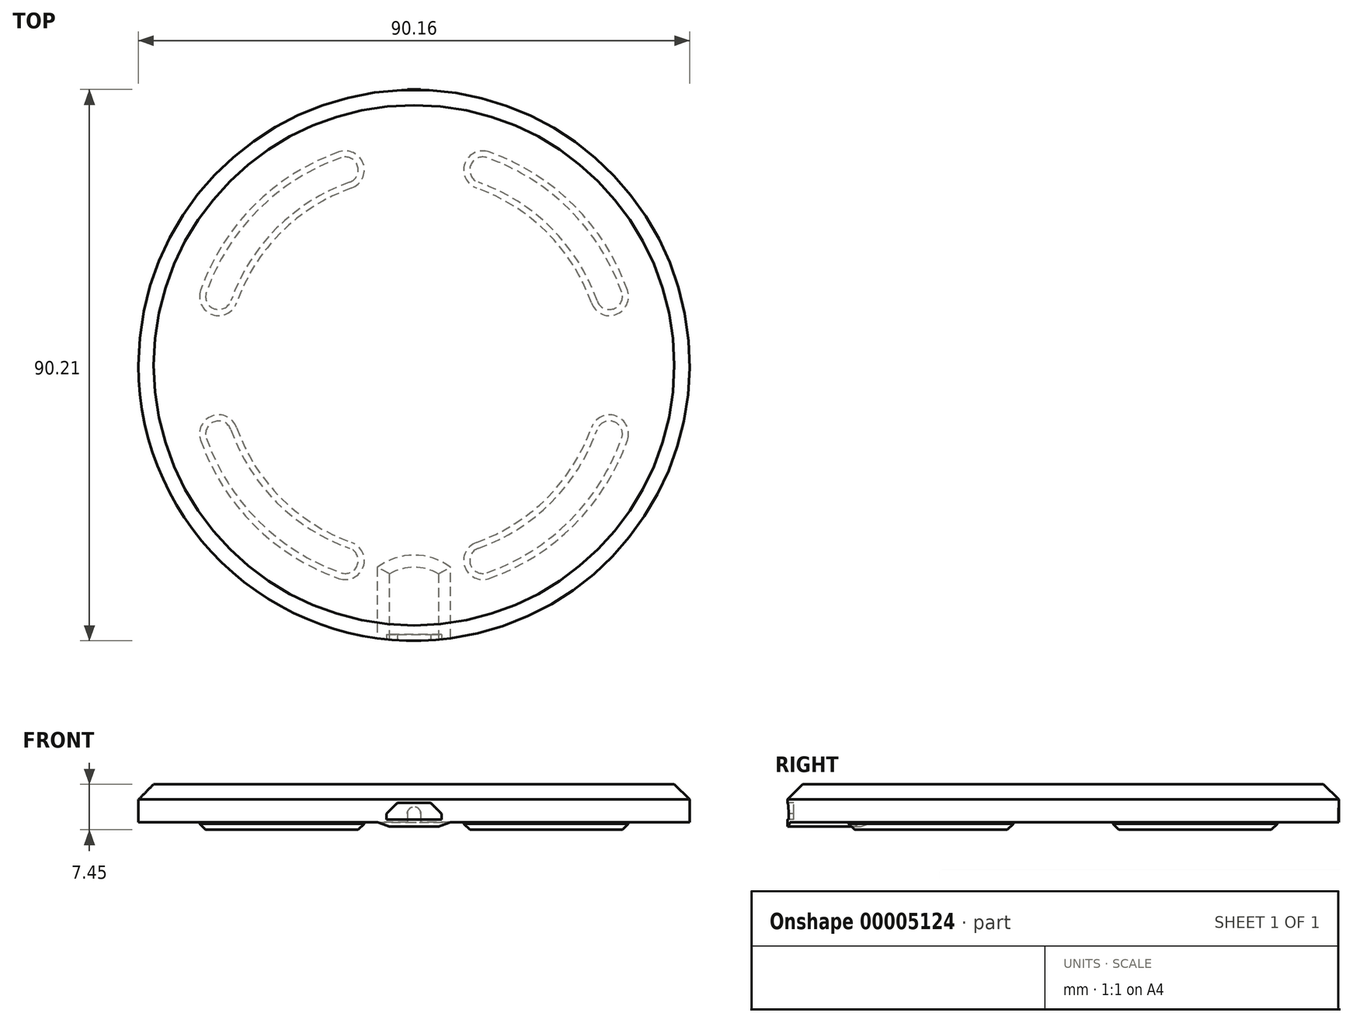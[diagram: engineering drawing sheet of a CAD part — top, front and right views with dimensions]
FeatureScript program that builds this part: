
annotation { "Feature Type Name" : "Feature", "Feature Type Description" : "" }
export const myFeature = defineFeature(function(context is Context, id is Id, definition is map)
    precondition{}
    {
        {
            var Q0;
            Q0=qCreatedBy(makeId("Top.planeOp"),FACE);
            var sketch = newSketch(context, id + "F0", { "sketchPlane" : qUnion([Q0])});
            skCircle(sketch, "E0", {"center": v(0, 0) * mm, "radius": 45.08 * mm});
            skSolve(sketch);
        }
        {
            var Q0;
            Q0 = qSketchRegion(id + "F0", true);
            extrude(context, id + "F1", {"entities" : qUnion([Q0]), "depth" : 6.2 * mm});
        }
        {
            var Q0;
            Q0=makeQuery(id+"F1.opExtrude","CAP_EDGE",EDGE,{"disambiguationData":[OSD([sQuery(id+"F0.wireOp",EDGE,"E0")])],"isStart":false});
            chamfer(context, id + "F2", {"entities" : qUnion([Q0]), "width" : 2.5 * mm, "tangentPropagation" : true});
        }
        {
            var Q0;
            Q0=makeQuery(id+"F1.opExtrude","CAP_FACE",FACE,{"disambiguationData":[OSD([sQuery(id+"F0.wireOp",EDGE,"E0")])],"isStart":true});
            var sketch = newSketch(context, id + "F3", { "sketchPlane" : qUnion([Q0])});
            skCircle(sketch, "E1", {"center": v(0, 0) * mm, "radius": 30.75 * mm});
            skCircle(sketch, "E2", {"center": v(0, 0) * mm, "radius": 37 * mm});
            skLineSegment(sketch, "E3", {"start": v(0, 37) * mm, "end": v(0, 30.75) * mm, "construction": true});
            skPoint(sketch, "E4", {"position": v(0, 30.75) * mm});
            skLineSegment(sketch, "E5", {"start": v(0, 30.75) * mm, "end": v(0, -45.08) * mm, "construction": true});
            skCircle(sketch, "E6", {"center": v(0, 33.88) * mm, "radius": 1 * mm});
            skLineSegment(sketch, "E7", {"start": v(-6, -44.67) * mm, "end": v(-6, -33.08) * mm});
            skLineSegment(sketch, "E8", {"start": v(6, -33.08) * mm, "end": v(6, -44.67) * mm});
            skArc(sketch, "E9", {"start": v(6, -33.08) * mm, "mid": v(0, -31.07) * mm, "end": v(-6, -33.08) * mm});
            skLineSegment(sketch, "E10", {"start": v(-6, -33.08) * mm, "end": v(6, -33.08) * mm, "construction": true});
            skLineSegment(sketch, "E11", {"start": v(0, 0) * mm, "end": v(-37, 0) * mm, "construction": true});
            skLineSegment(sketch, "E12", {"start": v(0, 0) * mm, "end": v(-26.16, 26.16) * mm, "construction": true});
            skLineSegment(sketch, "E13", {"start": v(-35.89, 9.01) * mm, "end": v(-29.82, 7.5) * mm, "construction": true});
            skPoint(sketch, "E14", {"position": v(-32.85, 8.25) * mm});
            skArc(sketch, "E15", {"start": v(-34.9, 12.28) * mm, "mid": v(-33, 8.3) * mm, "end": v(-29, 10.2) * mm});
            skArc(sketch, "E16.0.MirrorCS", {"start": v(-12.28, 34.9) * mm, "mid": v(-8.3, 33) * mm, "end": v(-10.2, 29) * mm});
            skArc(sketch, "E17.1.0", {"start": v(-12.28, -34.9) * mm, "mid": v(-8.3, -33) * mm, "end": v(-10.2, -29) * mm});
            skArc(sketch, "E17.1.1", {"start": v(-34.9, -12.28) * mm, "mid": v(-33, -8.3) * mm, "end": v(-29, -10.2) * mm});
            skArc(sketch, "E17.2.0", {"start": v(34.9, -12.28) * mm, "mid": v(33, -8.3) * mm, "end": v(29, -10.2) * mm});
            skArc(sketch, "E17.2.1", {"start": v(12.28, -34.9) * mm, "mid": v(8.3, -33) * mm, "end": v(10.2, -29) * mm});
            skArc(sketch, "E17.3.0", {"start": v(12.28, 34.9) * mm, "mid": v(8.3, 33) * mm, "end": v(10.2, 29) * mm});
            skArc(sketch, "E17.3.1", {"start": v(34.9, 12.28) * mm, "mid": v(33, 8.3) * mm, "end": v(29, 10.2) * mm});
            skSolve(sketch);
        }
        {
            var Q0;
            {var subQ1=sQuery(id+"F3.wireOp",EDGE,"E15");Q0=makeQuery(id+"F3.imprint","IMPRINT",FACE,{"disambiguationData":[TD([[makeQuery(id+"F3.imprint","IMPRINT",EDGE,{"derivedFrom":subQ1}),1.0]])]});}
            var Q1;
            {var subQ1=sQuery(id+"F3.wireOp",EDGE,"E17.1.0");Q1=makeQuery(id+"F3.imprint","IMPRINT",FACE,{"disambiguationData":[TD([[makeQuery(id+"F3.imprint","IMPRINT",EDGE,{"derivedFrom":subQ1}),1.0]])]});}
            var Q2;
            {var subQ1=sQuery(id+"F3.wireOp",EDGE,"E17.3.0");Q2=makeQuery(id+"F3.imprint","IMPRINT",FACE,{"disambiguationData":[TD([[makeQuery(id+"F3.imprint","IMPRINT",EDGE,{"derivedFrom":subQ1}),1.0]])]});}
            var Q3;
            {var subQ0=sQuery(id+"F3.wireOp",EDGE,"E17.2.0");Q3=makeQuery(id+"F3.imprint","IMPRINT",FACE,{"disambiguationData":[TD([[makeQuery(id+"F3.imprint","IMPRINT",EDGE,{"derivedFrom":subQ0}),1.0]])]});}
            extrude(context, id + "F4", {"entities" : qUnion([Q0, Q1, Q2, Q3]), "operationType" : NewBodyOperationType.ADD, "depth" : 1.25 * mm});
        }
        {
            var Q0;
            {var subQ0=sQuery(id+"F3.wireOp",EDGE,"E9");Q0=makeQuery(id+"F3.imprint","IMPRINT",FACE,{"disambiguationData":[TD([[makeQuery(id+"F3.imprint","IMPRINT",EDGE,{"derivedFrom":subQ0}),1.0]])]});}
            var Q1;
            {var subQ3=sQuery(id+"F3.wireOp",EDGE,"E7");var subQ5=sQuery(id+"F3.wireOp",EDGE,"E2");var subQ7=makeQuery(id+"F3.imprint","INTERSECT",VERTEX,{"derivedFrom":[subQ5,subQ3]});Q1=makeQuery(id+"F3.imprint","IMPRINT",FACE,{"disambiguationData":[TD([[makeQuery(id+"F3.imprint","IMPRINT",EDGE,{"disambiguationData":[TD([[subQ7,-1.0]])],"derivedFrom":subQ5}),-1.0]])]});}
            extrude(context, id + "F5", {"entities" : qUnion([Q0, Q1]), "operationType" : NewBodyOperationType.ADD, "depth" : 0.75 * mm});
        }
        {
            var Q0;
            Q0=makeQuery(id+"F5.opExtrude","CAP_EDGE",EDGE,{"disambiguationData":[OSD([sQuery(id+"F3.wireOp",EDGE,"E7")])],"isStart":false});
            var Q1;
            Q1=makeQuery(id+"F5.opExtrude","CAP_EDGE",EDGE,{"disambiguationData":[OSD([sQuery(id+"F3.wireOp",EDGE,"E9")])],"isStart":false});
            var Q2;
            Q2=makeQuery(id+"F5.opExtrude","CAP_EDGE",EDGE,{"disambiguationData":[OSD([sQuery(id+"F3.wireOp",EDGE,"E8")])],"isStart":false});
            chamfer(context, id + "F6", {"entities" : qUnion([Q0, Q1, Q2]), "chamferType" : ChamferType.TWO_OFFSETS, "width1" : 0.75 * mm, "oppositeDirection" : false, "width2" : 2 * mm, "tangentPropagation" : true});
        }
        {
            var Q0;
            Q0=qCreatedBy(makeId("Right.planeOp"),FACE);
            var sketch = newSketch(context, id + "F7", { "sketchPlane" : qUnion([Q0])});
            skLineSegment(sketch, "E18", {"start": v(45.08, 3.7) * mm, "end": v(45.08, -0.75) * mm, "construction": true});
            skLineSegment(sketch, "E19", {"start": v(-45.08, 3.7) * mm, "end": v(-45.08, 0) * mm, "construction": true});
            skSolve(sketch);
        }
        {
            var Q0;
            Q0=qCreatedBy(makeId("Front.planeOp"),FACE);
            var Q1;
            Q1=sQuery(id+"F7.wireOp",VERTEX,"E18.end");
            cPlane(context, id + "F8", {"entities" : qUnion([Q0, Q1]), "cplaneType" : CPlaneType.PLANE_POINT, "offset" : 150 * mm, "width" : 150 * mm, "height" : 150 * mm});
        }
        {
            var Q0;
            Q0=qCreatedBy(id+"F8.planeOp",FACE);
            var sketch = newSketch(context, id + "F9", { "sketchPlane" : qUnion([Q0])});
            skLineSegment(sketch, "E20.0", {"start": v(4, -0.75) * mm, "end": v(-4, -0.75) * mm});
            skFitSpline(sketch, "E20.1", {"points": [v(-6, 0) * mm, v(-5.33, -0.25) * mm, v(-4.67, -0.5) * mm, v(-4, -0.75) * mm]});
            skLineSegment(sketch, "E20.2", {"start": v(-45.08, 0) * mm, "end": v(45.08, 0) * mm});
            skFitSpline(sketch, "E20.3", {"points": [v(6, 0) * mm, v(5.33, -0.25) * mm, v(4.67, -0.5) * mm, v(4, -0.75) * mm]});
            skLineSegment(sketch, "E20.4", {"start": v(0, 3.7) * mm, "end": v(0, -0.75) * mm});
            skLineSegment(sketch, "E20.5", {"start": v(45.08, 3.7) * mm, "end": v(-45.08, 3.7) * mm});
            skLineSegment(sketch, "E20.6", {"start": v(-42.58, 6.2) * mm, "end": v(42.58, 6.2) * mm});
            skLineSegment(sketch, "E21", {"start": v(-4.5, 0.4) * mm, "end": v(4.5, 0.4) * mm});
            skLineSegment(sketch, "E22", {"start": v(4.5, 0.4) * mm, "end": v(4.5, 1.38) * mm});
            skLineSegment(sketch, "E23", {"start": v(4.5, 1.38) * mm, "end": v(2.73, 3.15) * mm});
            skLineSegment(sketch, "E24", {"start": v(2.73, 3.15) * mm, "end": v(-2.73, 3.15) * mm});
            skLineSegment(sketch, "E25", {"start": v(-2.73, 3.15) * mm, "end": v(-4.5, 1.38) * mm});
            skLineSegment(sketch, "E26", {"start": v(-4.5, 1.38) * mm, "end": v(-4.5, 0.4) * mm});
            skSolve(sketch);
        }
        {
            var Q0;
            {var subQ1=sQuery(id+"F9.wireOp",EDGE,"E25");Q0=makeQuery(id+"F9.imprint","IMPRINT",FACE,{"disambiguationData":[TD([[makeQuery(id+"F9.imprint","IMPRINT",EDGE,{"derivedFrom":subQ1}),1.0]])]});}
            var Q1;
            {var subQ4=sQuery(id+"F9.wireOp",EDGE,"E22");Q1=makeQuery(id+"F9.imprint","IMPRINT",FACE,{"disambiguationData":[TD([[makeQuery(id+"F9.imprint","IMPRINT",EDGE,{"derivedFrom":subQ4}),1.0]])]});}
            extrude(context, id + "F10", {"entities" : qUnion([Q0, Q1]), "operationType" : NewBodyOperationType.REMOVE, "depth" : 1 * mm});
        }
        {
            var Q0;
            Q0=qCreatedBy(makeId("Front.planeOp"),FACE);
            var Q1;
            Q1=sQuery(id+"F7.wireOp",VERTEX,"E19.end");
            cPlane(context, id + "F11", {"entities" : qUnion([Q0, Q1]), "cplaneType" : CPlaneType.PLANE_POINT, "offset" : 150 * mm, "width" : 150 * mm, "height" : 150 * mm});
        }
        {
            var Q0;
            Q0=qCreatedBy(id+"F11.planeOp",FACE);
            var sketch = newSketch(context, id + "F12", { "sketchPlane" : qUnion([Q0])});
            skLineSegment(sketch, "E27", {"start": v(0, 0) * mm, "end": v(-1.1, 0) * mm});
            skLineSegment(sketch, "E28", {"start": v(-1.1, 0) * mm, "end": v(-1.1, 1.4) * mm});
            skLineSegment(sketch, "E29", {"start": v(0, 0) * mm, "end": v(1.1, 0) * mm});
            skLineSegment(sketch, "E30", {"start": v(1.1, 0) * mm, "end": v(1.1, 1.4) * mm});
            skArc(sketch, "E31", {"start": v(1.1, 1.4) * mm, "mid": v(0, 2.5) * mm, "end": v(-1.1, 1.4) * mm});
            skSolve(sketch);
        }
        {
            var Q0;
            Q0=makeQuery(id+"F12.imprint","IMPRINT",FACE,{"disambiguationData":[TD([[makeQuery(id+"F12.imprint","IMPRINT",EDGE,{"derivedFrom":sQuery(id+"F12.wireOp",EDGE,"E27")}),-1.0]])]});
            extrude(context, id + "F13", {"entities" : qUnion([Q0]), "operationType" : NewBodyOperationType.ADD, "endBound" : BoundingType.SYMMETRIC, "depth" : 0.1 * mm});
        }
        {
            var Q0;
            Q0=makeQuery(id+"F4.opExtrude","CAP_FACE",FACE,{"disambiguationData":[OSD([sQuery(id+"F3.wireOp",EDGE,"E1"),sQuery(id+"F3.wireOp",EDGE,"E2"),sQuery(id+"F3.wireOp",EDGE,"E17.3.0"),sQuery(id+"F3.wireOp",EDGE,"E17.3.1")])],"isStart":false});
            var Q1;
            Q1=makeQuery(id+"F4.opExtrude","CAP_FACE",FACE,{"disambiguationData":[OSD([sQuery(id+"F3.wireOp",EDGE,"E1"),sQuery(id+"F3.wireOp",EDGE,"E2"),sQuery(id+"F3.wireOp",EDGE,"E15"),sQuery(id+"F3.wireOp",EDGE,"E16.0.MirrorCS")])],"isStart":false});
            var Q2;
            Q2=makeQuery(id+"F4.opExtrude","CAP_FACE",FACE,{"disambiguationData":[OSD([sQuery(id+"F3.wireOp",EDGE,"E1"),sQuery(id+"F3.wireOp",EDGE,"E2"),sQuery(id+"F3.wireOp",EDGE,"E17.1.0"),sQuery(id+"F3.wireOp",EDGE,"E17.1.1")])],"isStart":false});
            var Q3;
            Q3=makeQuery(id+"F4.opExtrude","CAP_FACE",FACE,{"disambiguationData":[OSD([sQuery(id+"F3.wireOp",EDGE,"E1"),sQuery(id+"F3.wireOp",EDGE,"E2"),sQuery(id+"F3.wireOp",EDGE,"E17.2.0"),sQuery(id+"F3.wireOp",EDGE,"E17.2.1")])],"isStart":false});
            chamfer(context, id + "F14", {"entities" : qUnion([Q0, Q1, Q2, Q3]), "width" : 1 * mm, "tangentPropagation" : true});
        }
        {
            var Q0;
            Q0=qCreatedBy(makeId("Right.planeOp"),FACE);
            var sketch = newSketch(context, id + "F15", { "sketchPlane" : qUnion([Q0])});
            skLineSegment(sketch, "E32", {"start": v(0, 0) * mm, "end": v(0, 24.28) * mm, "construction": true});
            skSolve(sketch);
        }
        {
            var Q0;
            Q0=makeQuery(id+"F1.opExtrude","SWEPT_BODY",BODY,{"disambiguationData":[OSD([sQuery(id+"F0.wireOp",EDGE,"E0")])]});
            var Q1;
            Q1=sQuery(id+"F15.wireOp",EDGE,"E32");
            transform(context, id + "F16", {"entities" : qUnion([Q0]), "transformType" : TransformType.ROTATION, "transformAxis" : qUnion([Q1]), "angle" : 180 * degree, "makeCopy" : false});
        }
    });
